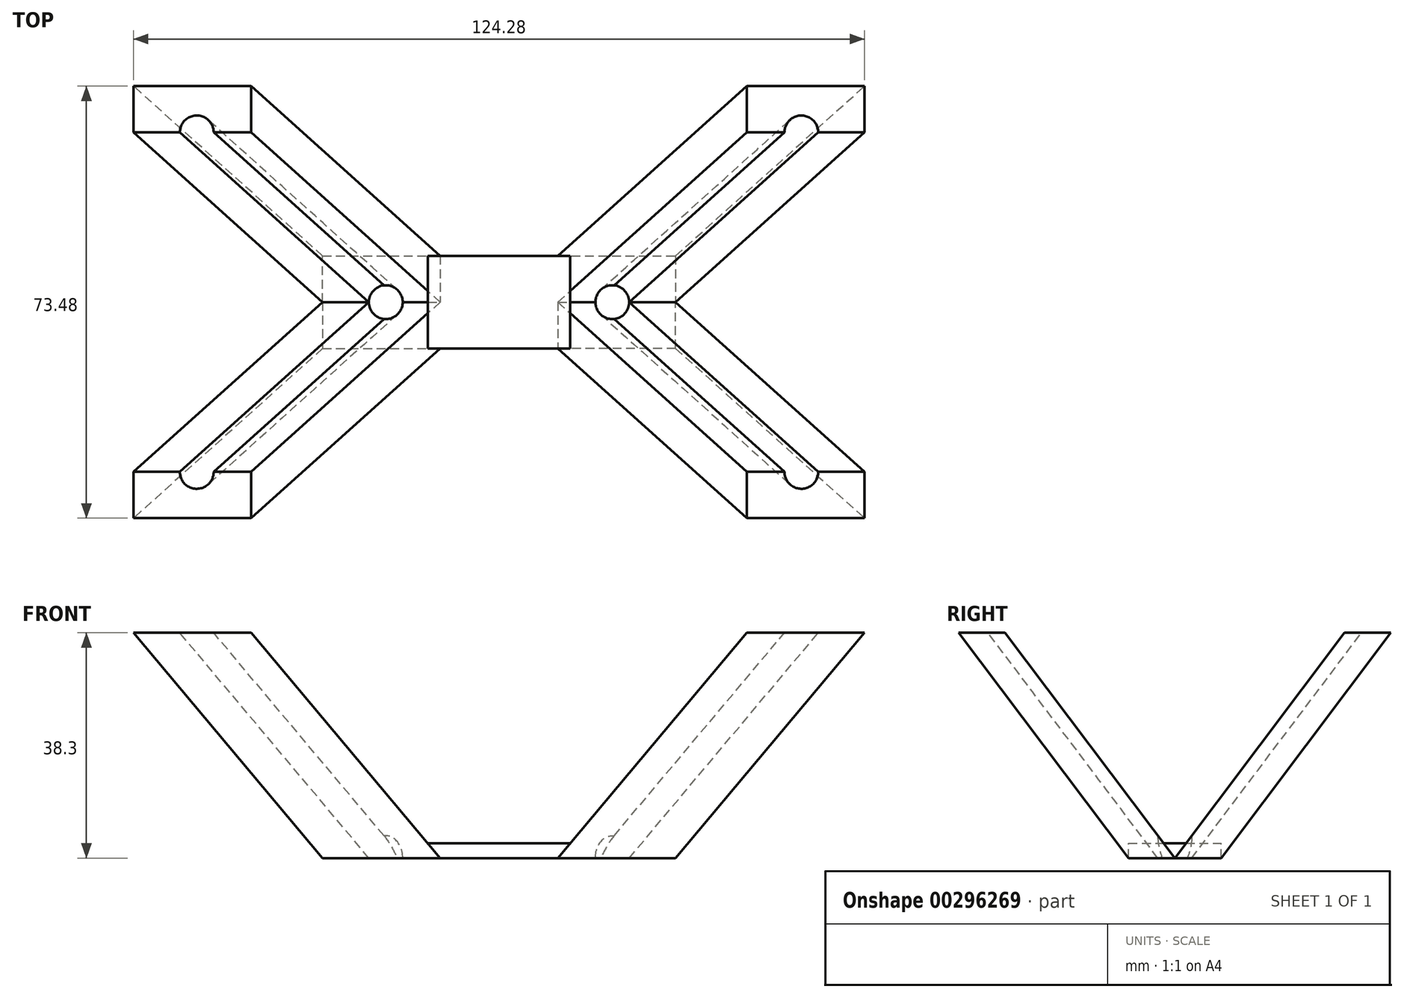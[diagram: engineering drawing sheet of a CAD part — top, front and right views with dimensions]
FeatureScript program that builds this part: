
annotation { "Feature Type Name" : "Feature", "Feature Type Description" : "" }
export const myFeature = defineFeature(function(context is Context, id is Id, definition is map)
    precondition{}
    {
        {
            var Q0;
            Q0=qCreatedBy(makeId("Top.planeOp"),FACE);
            var sketch = newSketch(context, id + "F0", { "sketchPlane" : qUnion([Q0])});
            skLineSegment(sketch, "E0", {"start": v(-19.25, 0) * mm, "end": v(19.25, 0) * mm});
            skCircle(sketch, "E1", {"center": v(-19.25, 0) * mm, "radius": 2.88 * mm});
            skCircle(sketch, "E2", {"center": v(19.25, 0) * mm, "radius": 2.88 * mm});
            skLineSegment(sketch, "E3", {"start": v(-19.25, 0) * mm, "end": v(-30, 0) * mm});
            skLineSegment(sketch, "E4", {"start": v(19.25, 0) * mm, "end": v(30, 0) * mm});
            skLineSegment(sketch, "E5", {"start": v(0, 0) * mm, "end": v(0, 7.87) * mm});
            skLineSegment(sketch, "E6", {"start": v(0, 0) * mm, "end": v(0, -7.87) * mm});
            skLineSegment(sketch, "E7", {"start": v(0, 7.87) * mm, "end": v(30, 7.87) * mm});
            skLineSegment(sketch, "E8", {"start": v(30, 7.87) * mm, "end": v(30, 0) * mm});
            skLineSegment(sketch, "E9", {"start": v(30, -7.87) * mm, "end": v(30, 0) * mm});
            skLineSegment(sketch, "E10", {"start": v(30, -7.87) * mm, "end": v(0, -7.88) * mm});
            skLineSegment(sketch, "E11", {"start": v(-30, 0) * mm, "end": v(-30, -7.87) * mm});
            skLineSegment(sketch, "E12", {"start": v(-30, -7.88) * mm, "end": v(0, -7.88) * mm});
            skLineSegment(sketch, "E13", {"start": v(-30, 0) * mm, "end": v(-30, 7.87) * mm});
            skLineSegment(sketch, "E14", {"start": v(-30, 7.87) * mm, "end": v(0, 7.87) * mm});
            skLineSegment(sketch, "E15", {"start": v(0, 15.25) * mm, "end": v(-10, 15.25) * mm});
            skLineSegment(sketch, "E16", {"start": v(-10, 7.88) * mm, "end": v(-10, -7.88) * mm});
            skLineSegment(sketch, "E17.MirrorCS", {"start": v(10, 7.88) * mm, "end": v(10, -7.88) * mm});
            skSolve(sketch);
        }
        {
            var Q0;
            {var subQ0=sQuery(id+"F0.wireOp",EDGE,"E5");Q0=makeQuery(id+"F0.imprint","IMPRINT",FACE,{"disambiguationData":[TD([[makeQuery(id+"F0.imprint","IMPRINT",EDGE,{"derivedFrom":subQ0}),1.0]])]});}
            var Q1;
            {var subQ6=sQuery(id+"F0.wireOp",EDGE,"E5");Q1=makeQuery(id+"F0.imprint","IMPRINT",FACE,{"disambiguationData":[TD([[makeQuery(id+"F0.imprint","IMPRINT",EDGE,{"derivedFrom":subQ6}),-1.0]])]});}
            var Q2;
            {var subQ0=sQuery(id+"F0.wireOp",EDGE,"E6");Q2=makeQuery(id+"F0.imprint","IMPRINT",FACE,{"disambiguationData":[TD([[makeQuery(id+"F0.imprint","IMPRINT",EDGE,{"derivedFrom":subQ0}),1.0]])]});}
            var Q3;
            {var subQ0=sQuery(id+"F0.wireOp",EDGE,"E6");Q3=makeQuery(id+"F0.imprint","IMPRINT",FACE,{"disambiguationData":[TD([[makeQuery(id+"F0.imprint","IMPRINT",EDGE,{"derivedFrom":subQ0}),-1.0]])]});}
            extrude(context, id + "F1", {"entities" : qUnion([Q0, Q1, Q2, Q3]), "depth" : 2.5 * mm, "offsetDistance" : 25 * mm});
        }
        {
            var Q0;
            Q0=qCreatedBy(makeId("Front.planeOp"),FACE);
            var sketch = newSketch(context, id + "F2", { "sketchPlane" : qUnion([Q0])});
            skLineSegment(sketch, "E18", {"start": v(0, 0) * mm, "end": v(-10, 0) * mm});
            skLineSegment(sketch, "E19", {"start": v(0, 0) * mm, "end": v(10, 0) * mm});
            skLineSegment(sketch, "E20", {"start": v(10, 0) * mm, "end": v(42.14, 38.3) * mm});
            skLineSegment(sketch, "E21", {"start": v(-10, 0) * mm, "end": v(-42.14, 38.3) * mm});
            skSolve(sketch);
        }
        {
            var Q0;
            Q0=sQuery(id+"F2.wireOp",EDGE,"E21");
            cPlane(context, id + "F3", {"entities" : qUnion([Q0]), "cplaneType" : CPlaneType.LINE_ANGLE, "offset" : 25 * mm, "angle" : 0 * degree, "width" : 150 * mm, "height" : 150 * mm});
        }
        {
            var Q0;
            Q0=qCreatedBy(id+"F3.planeOp",FACE);
            var sketch = newSketch(context, id + "F4", { "sketchPlane" : qUnion([Q0])});
            skLineSegment(sketch, "E22", {"start": v(0, 6.64) * mm, "end": v(0, 56.64) * mm});
            skLineSegment(sketch, "E23", {"start": v(0, 56.64) * mm, "end": v(28.87, 56.64) * mm});
            skLineSegment(sketch, "E24", {"start": v(28.87, 56.64) * mm, "end": v(0, 6.64) * mm});
            skLineSegment(sketch, "E25.MirrorCS", {"start": v(0, 56.64) * mm, "end": v(-28.87, 56.64) * mm});
            skLineSegment(sketch, "E26.MirrorCS", {"start": v(-28.87, 56.64) * mm, "end": v(0, 6.64) * mm});
            skSolve(sketch);
        }
        {
            var Q0;
            {var subQ0=sQuery(id+"F0.wireOp",EDGE,"E13");Q0=makeQuery(id+"F0.imprint","IMPRINT",FACE,{"disambiguationData":[TD([[makeQuery(id+"F0.imprint","IMPRINT",EDGE,{"derivedFrom":subQ0}),-1.0]])]});}
            var Q1;
            Q1=sQuery(id+"F4.wireOp",EDGE,"E24");
            sweep(context, id + "F5", {"operationType" : NewBodyOperationType.ADD, "profiles" : qUnion([Q0]), "path" : qUnion([Q1])});
        }
        {
            var Q0;
            Q0=sQuery(id+"F2.wireOp",EDGE,"E20");
            cPlane(context, id + "F6", {"entities" : qUnion([Q0]), "cplaneType" : CPlaneType.LINE_ANGLE, "offset" : 25 * mm, "angle" : 0 * degree, "width" : 150 * mm, "height" : 150 * mm});
        }
        {
            var Q0;
            Q0=qCreatedBy(id+"F6.planeOp",FACE);
            var sketch = newSketch(context, id + "F7", { "sketchPlane" : qUnion([Q0])});
            skLineSegment(sketch, "E27", {"start": v(0, 6.54) * mm, "end": v(0, 56.54) * mm});
            skLineSegment(sketch, "E28", {"start": v(0, 56.54) * mm, "end": v(-28.87, 56.54) * mm});
            skLineSegment(sketch, "E29", {"start": v(-28.87, 56.54) * mm, "end": v(0, 6.54) * mm});
            skLineSegment(sketch, "E30.MirrorCS", {"start": v(28.87, 56.54) * mm, "end": v(0, 6.54) * mm});
            skLineSegment(sketch, "E31.MirrorCS", {"start": v(0, 56.54) * mm, "end": v(28.87, 56.54) * mm});
            skSolve(sketch);
        }
        {
            var Q0;
            {var subQ0=sQuery(id+"F0.wireOp",EDGE,"E11");Q0=makeQuery(id+"F0.imprint","IMPRINT",FACE,{"disambiguationData":[TD([[makeQuery(id+"F0.imprint","IMPRINT",EDGE,{"derivedFrom":subQ0}),1.0]])]});}
            var Q1;
            Q1=sQuery(id+"F4.wireOp",EDGE,"E26.MirrorCS");
            sweep(context, id + "F8", {"operationType" : NewBodyOperationType.ADD, "profiles" : qUnion([Q0]), "path" : qUnion([Q1])});
        }
        {
            var Q0;
            {var subQ0=sQuery(id+"F0.wireOp",EDGE,"E9");Q0=makeQuery(id+"F0.imprint","IMPRINT",FACE,{"disambiguationData":[TD([[makeQuery(id+"F0.imprint","IMPRINT",EDGE,{"derivedFrom":subQ0}),1.0]])]});}
            var Q1;
            Q1=sQuery(id+"F7.wireOp",EDGE,"E29");
            sweep(context, id + "F9", {"operationType" : NewBodyOperationType.ADD, "profiles" : qUnion([Q0]), "path" : qUnion([Q1])});
        }
        {
            var Q0;
            {var subQ0=sQuery(id+"F0.wireOp",EDGE,"E8");Q0=makeQuery(id+"F0.imprint","IMPRINT",FACE,{"disambiguationData":[TD([[makeQuery(id+"F0.imprint","IMPRINT",EDGE,{"derivedFrom":subQ0}),-1.0]])]});}
            var Q1;
            Q1=sQuery(id+"F7.wireOp",EDGE,"E30.MirrorCS");
            sweep(context, id + "F10", {"operationType" : NewBodyOperationType.ADD, "profiles" : qUnion([Q0]), "path" : qUnion([Q1])});
        }
        {
            var Q0;
            {var subQ0=sQuery(id+"F0.wireOp",EDGE,"E4");var subQ1=sQuery(id+"F0.wireOp",EDGE,"E0");var subQ2=makeQuery(id+"F0.imprint","INTERSECT",VERTEX,{"derivedFrom":[subQ1,subQ0]});Q0=makeQuery(id+"F0.imprint","IMPRINT",FACE,{"disambiguationData":[TD([[makeQuery(id+"F0.imprint","IMPRINT",EDGE,{"disambiguationData":[TD([[subQ2,1.0]])],"derivedFrom":subQ1}),-1.0]])]});}
            var Q1;
            {var subQ0=sQuery(id+"F0.wireOp",EDGE,"E4");var subQ1=sQuery(id+"F0.wireOp",EDGE,"E0");var subQ2=makeQuery(id+"F0.imprint","INTERSECT",VERTEX,{"derivedFrom":[subQ1,subQ0]});Q1=makeQuery(id+"F0.imprint","IMPRINT",FACE,{"disambiguationData":[TD([[makeQuery(id+"F0.imprint","IMPRINT",EDGE,{"disambiguationData":[TD([[subQ2,1.0]])],"derivedFrom":subQ1}),1.0]])]});}
            var Q2;
            {var subQ0=sQuery(id+"F0.wireOp",EDGE,"E3");var subQ1=sQuery(id+"F0.wireOp",EDGE,"E0");var subQ2=makeQuery(id+"F0.imprint","INTERSECT",VERTEX,{"derivedFrom":[subQ1,subQ0]});Q2=makeQuery(id+"F0.imprint","IMPRINT",FACE,{"disambiguationData":[TD([[makeQuery(id+"F0.imprint","IMPRINT",EDGE,{"disambiguationData":[TD([[subQ2,-1.0]])],"derivedFrom":subQ1}),1.0]])]});}
            var Q3;
            {var subQ0=sQuery(id+"F0.wireOp",EDGE,"E3");var subQ1=sQuery(id+"F0.wireOp",EDGE,"E0");var subQ2=makeQuery(id+"F0.imprint","INTERSECT",VERTEX,{"derivedFrom":[subQ1,subQ0]});Q3=makeQuery(id+"F0.imprint","IMPRINT",FACE,{"disambiguationData":[TD([[makeQuery(id+"F0.imprint","IMPRINT",EDGE,{"disambiguationData":[TD([[subQ2,-1.0]])],"derivedFrom":subQ1}),-1.0]])]});}
            extrude(context, id + "F11", {"entities" : qUnion([Q0, Q1, Q2, Q3]), "operationType" : NewBodyOperationType.REMOVE, "depth" : 25 * mm, "offsetDistance" : 25 * mm});
        }
        {
            var Q0;
            Q0=qCreatedBy(makeId("Front.planeOp"),FACE);
            var sketch = newSketch(context, id + "F12", { "sketchPlane" : qUnion([Q0])});
            skLineSegment(sketch, "E32", {"start": v(0, 0) * mm, "end": v(-10, 0) * mm});
            skLineSegment(sketch, "E33", {"start": v(-10, 0) * mm, "end": v(-10, 2.5) * mm});
            skLineSegment(sketch, "E34", {"start": v(-10, 0) * mm, "end": v(-12.1, 2.5) * mm});
            skLineSegment(sketch, "E35", {"start": v(-12.1, 2.5) * mm, "end": v(-10, 2.5) * mm});
            skLineSegment(sketch, "E36.MirrorCS", {"start": v(10, 0) * mm, "end": v(10, 2.5) * mm});
            skLineSegment(sketch, "E37.MirrorCS", {"start": v(12.1, 2.5) * mm, "end": v(10, 2.5) * mm});
            skLineSegment(sketch, "E38.MirrorCS", {"start": v(10, 0) * mm, "end": v(12.1, 2.5) * mm});
            skSolve(sketch);
        }
        {
            var Q0;
            Q0=makeQuery(id+"F12.imprint","IMPRINT",FACE,{"disambiguationData":[TD([[makeQuery(id+"F12.imprint","IMPRINT",EDGE,{"derivedFrom":sQuery(id+"F12.wireOp",EDGE,"E36.MirrorCS")}),-1.0]])]});
            var Q1;
            Q1=makeQuery(id+"F12.imprint","IMPRINT",FACE,{"disambiguationData":[TD([[makeQuery(id+"F12.imprint","IMPRINT",EDGE,{"derivedFrom":sQuery(id+"F12.wireOp",EDGE,"E33")}),1.0]])]});
            extrude(context, id + "F13", {"entities" : qUnion([Q0, Q1]), "operationType" : NewBodyOperationType.ADD, "depth" : (5 + (11.5 / 4)) * mm, "offsetDistance" : 25 * mm, "hasSecondDirection" : true, "secondDirectionOppositeDirection" : true, "secondDirectionDepth" : (5 + (11.5 / 4)) * mm});
        }
    });
